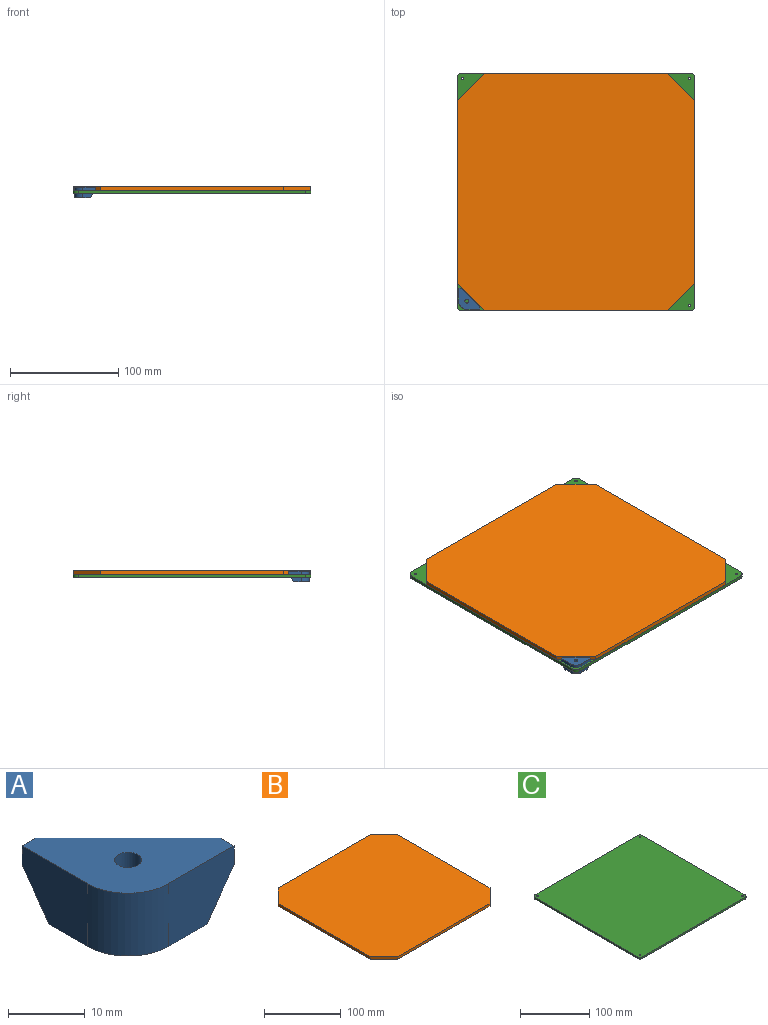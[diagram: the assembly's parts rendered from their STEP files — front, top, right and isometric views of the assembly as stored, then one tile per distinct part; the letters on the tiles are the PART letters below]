
ASSEMBLY  parts=3 mates=5
PART A: 15 faces, bbox 19.5x19.5x10 mm
  f0: plane 17x17mm, normal (0.71,0.71,0), area 72.1mm2, adj f1,f2,f7,f9
  f1: plane 19.5x19.5mm, normal (0,0,1), area 214.1mm2, adj f0,f3,f6,f7,f9,f10,f11
  f2: plane 17x17mm, normal (0,0,-1), area 129.5mm2, adj f0,f3,f4,f5,f8
  f3: cylinder r=1.75mm len=3.5mm, axis (0,0,1), area 33mm2, adj f1,f2
  f4: plane 12x7mm, normal (1,0,0), area 66.5mm2, adj f2,f8,f12,f13
  f5: plane 12x7mm, normal (0,1,0), area 66.5mm2, adj f2,f8,f12,f14
  f6: plane 12x10mm, normal (0,-1,0), area 102.5mm2, adj f1,f7,f11,f12,f14
  f7: plane 3x2.5mm, normal (1,0,0), area 7.5mm2, adj f0,f1,f6,f14
  f8: cylinder r=5mm len=7mm, axis (0,0,1), area 55mm2, adj f2,f4,f5,f12
  f9: plane 3x2.5mm, normal (0,1,0), area 7.5mm2, adj f0,f1,f10,f13
  f10: plane 12x10mm, normal (-1,0,0), area 102.5mm2, adj f1,f9,f11,f12,f13
  f11: cylinder r=7.5mm len=10mm, axis (0,0,1), area 117.8mm2, adj f1,f6,f10,f12
  f12: plane 14.5x14.5mm, normal (0,0,-1), area 59.5mm2, adj f4,f5,f6,f8,f10,f11,f13,f14
  f13: plane 7x5mm, normal (0,0.81,-0.58), area 21.5mm2, adj f4,f9,f10,f12
  f14: plane 7x5mm, normal (0.81,0,-0.58), area 21.5mm2, adj f5,f6,f7,f12
PART B: 10 faces, bbox 220x220x4 mm
  f0: plane 170x4mm, normal (-1,0,0), area 680mm2, adj f4,f5,f7,f8
  f1: plane 170x4mm, normal (0,-1,0), area 680mm2, adj f4,f5,f8,f9
  f2: plane 170x4mm, normal (1,0,0), area 680mm2, adj f4,f5,f6,f9
  f3: plane 170x4mm, normal (0,1,0), area 680mm2, adj f4,f5,f6,f7
  f4: plane 220x220mm, normal (0,0,1), area 47150mm2, adj f0,f1,f2,f3,f6,f7,f8,f9
  f5: plane 220x220mm, normal (0,0,-1), area 47150mm2, adj f0,f1,f2,f3,f6,f7,f8,f9
  f6: plane 25x25mm, normal (0.71,0.71,0), area 141.4mm2, adj f2,f3,f4,f5
  f7: plane 25x25mm, normal (-0.71,0.71,0), area 141.4mm2, adj f0,f3,f4,f5
  f8: plane 25x25mm, normal (-0.71,-0.71,0), area 141.4mm2, adj f0,f1,f4,f5
  f9: plane 25x25mm, normal (0.71,-0.71,0), area 141.4mm2, adj f1,f2,f4,f5
PART C: 14 faces, bbox 220x220x3 mm
  f0: plane 220x220mm, normal (0,0,1), area 48358.9mm2, adj f2,f3,f4,f5,f6,f7,f8,f9
  f1: plane 220x220mm, normal (0,0,-1), area 48358.9mm2, adj f2,f3,f4,f5,f6,f7,f8,f9
  f2: plane 210x3mm, normal (-1,0,0), area 630mm2, adj f0,f1,f10,f13
  f3: plane 210x3mm, normal (0,-1,0), area 630mm2, adj f0,f1,f10,f11
  f4: plane 210x3mm, normal (1,0,0), area 630mm2, adj f0,f1,f11,f12
  f5: plane 210x3mm, normal (0,1,0), area 630mm2, adj f0,f1,f12,f13
  f6: cylinder r=1.25mm len=3mm, axis (0,0,1), area 23.6mm2, adj f0,f1
  f7: cylinder r=1.25mm len=3mm, axis (0,0,1), area 23.6mm2, adj f0,f1
  f8: cylinder r=1.25mm len=3mm, axis (0,0,1), area 23.6mm2, adj f0,f1
  f9: cylinder r=1.25mm len=3mm, axis (0,0,1), area 23.6mm2, adj f0,f1
  f10: cylinder r=5mm len=5mm, axis (0,0,1), area 23.6mm2, adj f0,f1,f2,f3
  f11: cylinder r=5mm len=5mm, axis (0,0,-1), area 23.6mm2, adj f0,f1,f3,f4
  f12: cylinder r=5mm len=5mm, axis (0,0,1), area 23.6mm2, adj f0,f1,f4,f5
  f13: cylinder r=5mm len=5mm, axis (0,0,-1), area 23.6mm2, adj f0,f1,f2,f5
PLACE A t=(-97.5,-97.5,3)mm
PLACE B t=(0,0,3)mm
PLACE C at identity fixed
MATE planar B.f1 <-> C.f3  axis (0,-1,0) through (0,-110,5)mm
MATE planar B.f2 <-> C.f4  axis (1,0,0) through (110,0,5)mm
MATE planar A.f0 <-> B.f8  axis (0.71,0.71,0) through (-97.5,-97.5,4.5)mm
MATE planar C.f0 <-> B.f5  axis (0,0,1) through (0,0,3)mm
MATE planar A.f2 <-> C.f0  axis (0,0,-1) through (-100.1,-100.1,3)mm
